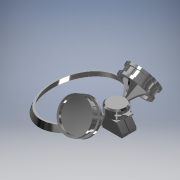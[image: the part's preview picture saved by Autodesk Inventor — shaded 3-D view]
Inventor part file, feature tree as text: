
AUTODESK INVENTOR PART (.ipt)
format: ipt  version: 2021 (Build 250183000, 183)  size: 794,624 bytes
history: native  units: in
note: dims shown in document units (in); Inventor stores cm internally (conversion verified against a paired STEP export)
features: extrude x21, sketch x19, plane x10, mirror x5, fillet x3, loft x2, chamfer x1, other x1, pattern_circular x1
ambient origin geometry x8: Origin, YZ Plane, XZ Plane, XY Plane, X Axis, Y Axis, Z Axis, Center Point
bodies: Solid1 (feature_tree)
feature tree (63):
  extrude  "Extrusion1"  Depth=1.15in
  extrude  "Extrusion2"  Depth=2.0in TaperAngle=0.0deg
  extrude  "Extrusion3"  Depth=0.05in TaperAngle=0.0deg
  extrude  "Extrusion4"  Depth=0.4in
  chamfer  "Chamfer1"  Distance=0.65in
  extrude  "Extrusion5"  Depth=0.01in TaperAngle=0.0deg
  extrude  "Extrusion6"  Depth=1.0in TaperAngle=0.0deg
  extrude  "Extrusion7"  Depth=0.1in TaperAngle=0.0deg
  plane  "Work Plane1"
  extrude  "Extrusion8"  Depth=0.06in
  extrude  "Extrusion9"  Depth=0.026in
  extrude  "Extrusion10"  Depth=0.8in TaperAngle=0.0deg
  extrude  "Extrusion11"  TaperAngle=60.0deg  [1 undecoded]
  fillet  "Fillet1"  Radius=0.075in
  fillet  "Fillet2"  Radius=0.1in
  fillet  "Fillet3"  Radius=1.441in
  extrude  "Extrusion12"  Depth=0.1092in
  extrude  "Extrusion13"  Depth=0.72in
  extrude  "Extrusion14"  Depth=0.1in TaperAngle=0.0deg
  plane  "Work Plane2"
  extrude  "Extrusion15"  Depth=0.15in TaperAngle=0.0deg
  plane  "Work Plane3"
  mirror  "Mirror1"
  plane  "Work Plane4"
  extrude  "Extrusion16"  [1 undecoded]
  plane  "Work Plane5"
  mirror  "Mirror2"
  plane  "Work Plane6"
  sketch  "Sketch17"  dims[d29=0.2in d30=0.0in d31=0.06in]
  extrude  "Extrusion17"  Depth=0.5in TaperAngle=0.0deg
  mirror  "Mirror3"
  extrude  "Extrusion18"  [1 undecoded]
  extrude  "Extrusion19"  TaperAngle=0.0deg  [1 undecoded]
  extrude  "Extrusion20"  TaperAngle=0.0deg  [1 undecoded]
  mirror  "Mirror4"
  plane  "Work Plane7"
  extrude  "Extrusion22"  TaperAngle=0.0deg  [1 undecoded]
  other  "Work Axis1"
  pattern_circular  "Circular Pattern1"  Angle=90.0deg  [1 undecoded]
  plane  "Work Plane8"
  mirror  "Mirror5"
  sketch  "Sketch25"  dims[d51=0.109in d52=0.1in d53=0.0in]
  sketch  "Sketch26"  dims[d54=0.35in d55=0.0in d56=0.15in d57=0.0in]
  plane  "Work Plane9"
  plane  "Work Plane10"
  loft  "Loft1"
  loft  "Loft2"
  sketch  "Sketch1"  dims[d0=0.85in d1=1.15in]
  sketch  "Sketch8"  dims[d2=0.65in d3=0.0in d4=2.0in d5=0.0in]
  sketch  "Sketch10"  dims[d6=0.6in d7=0.0in d8=0.05in d9=0.0in]
  sketch  "Sketch12"  dims[d10=0.075in d11=0.125in d12=45.0deg d13=0.4in]
  sketch  "Sketch13"  dims[d14=0.4in d15=0.65in d16=0.0in]
  sketch  "Sketch14"  dims[d18=0.1in d19=0.0in d20=0.01in d21=0.0in]
  sketch  "Sketch15"  dims[d22=0.0in d23=1.0in d24=0.0in]
  sketch  "Sketch16"  dims[d25=1.0in d26=0.0in d27=0.1in d28=0.0in]
  sketch  "Sketch18"  dims[d32=0.03in d33=0.026in]
  sketch  "Sketch19"  dims[d34=0.8in d35=0.0in d36=0.8in d37=0.0in]
  sketch  "Sketch21"  dims[d38=0.8in d39=0.0in d40=60.0deg d41=0.075in d42=0.0in d43=0.1in d44=0.0in d45=1.441in]
  sketch  "Sketch22"  dims[d46=1.208in d47=0.1092in]
  sketch  "Sketch24"  dims[d48=1.0606in d50=0.72in]
  sketch  "Sketch28"  dims[d58=0.15in d59=0.0in d60=-0.05in]
  sketch  "Sketch29"  dims[d63=4.7244in d65=360.0deg d67=0.5in d68=0.0in]
  sketch  "Sketch30"  dims[d69=3.937in d70=360.0deg d72=-0.25in d73=-0.35in d74=0.0in d75=90.0deg d76=0.0in d77=90.0deg d78=0.0in d79=90.0deg d80=0.0in d81=90.0deg]
note: 7 required parameter values undecoded (feature->parameter linkage not recoverable at this tier; creation-order binding heuristic only, values carry confidence <= 0.55)
